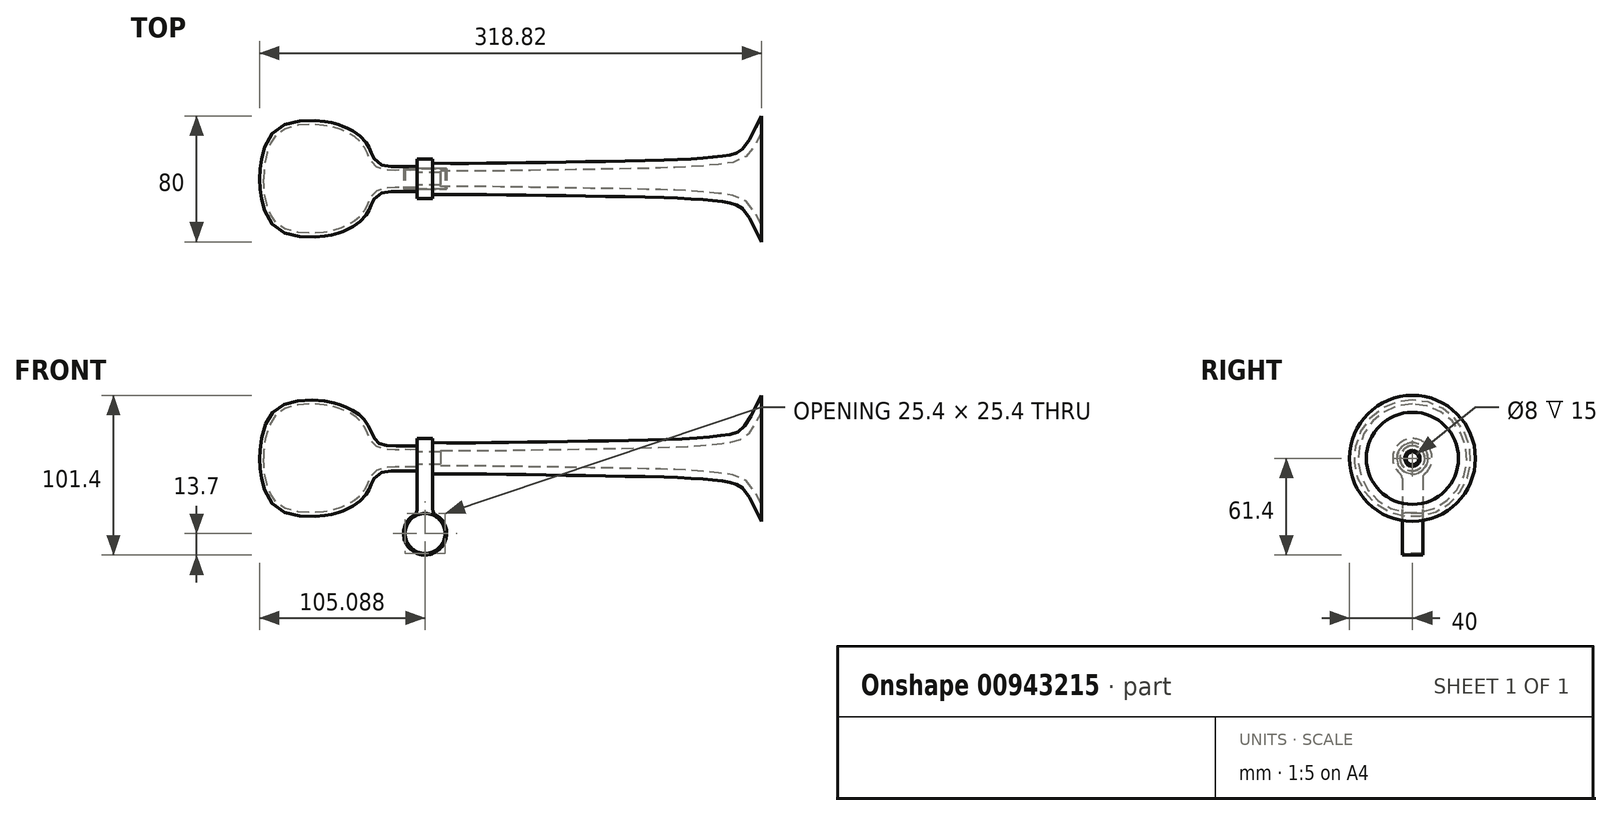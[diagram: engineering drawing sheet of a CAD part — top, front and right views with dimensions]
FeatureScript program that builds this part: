
annotation { "Feature Type Name" : "Feature", "Feature Type Description" : "" }
export const myFeature = defineFeature(function(context is Context, id is Id, definition is map)
    precondition{}
    {
        {
            var Q0;
            Q0=qCreatedBy(makeId("Front.planeOp"),FACE);
            var sketch = newSketch(context, id + "F0", { "sketchPlane" : qUnion([Q0])});
            skLineSegment(sketch, "E0", {"start": v(0, 0) * mm, "end": v(211.18, 0) * mm, "construction": true});
            skLineSegment(sketch, "E1", {"start": v(0, 0) * mm, "end": v(0, 10) * mm});
            skFitSpline(sketch, "E2", {"points": [v(0, 10) * mm, v(36.9, 10) * mm, v(101.92, 11) * mm, v(161.13, 12.56) * mm, v(186.25, 14.85) * mm, v(197.59, 19.9) * mm, v(208.82, 40) * mm, v(215.57, 39.65) * mm], "startDerivative": vector(222.11, -4.41) * mm, "endDerivative": vector(139.53, -179.69) * mm});
            skLineSegment(sketch, "E3", {"start": v(208.82, 40) * mm, "end": v(208.82, 0) * mm});
            skLineSegment(sketch, "E4", {"start": v(0, 0) * mm, "end": v(208.82, 0) * mm});
            skSolve(sketch);
        }
        {
            var Q0;
            Q0=qSketchRegion(id+"F0",true);
            var Q1;
            Q1=sQuery(id+"F0.wireOp",EDGE,"E0");
            revolve(context, id + "F1", {"surfaceOperationType" : NewSurfaceOperationType.NEW, "entities" : qUnion([Q0]), "axis" : qUnion([Q1]), "revolveType" : RevolveType.FULL});
        }
        {
            var Q0;
            Q0=makeQuery(id+"F1.opRevolve","SWEPT_FACE",FACE,{"disambiguationData":[OSD([sQuery(id+"F0.wireOp",EDGE,"E3")])]});
            shell(context, id + "F2", {"entities" : qUnion([Q0]), "thickness" : 5 * mm});
        }
        {
            var Q0;
            Q0=makeQuery(id+"F1.opRevolve","SWEPT_FACE",FACE,{"disambiguationData":[OSD([sQuery(id+"F0.wireOp",EDGE,"E1")])]});
            var sketch = newSketch(context, id + "F3", { "sketchPlane" : qUnion([Q0])});
            skPoint(sketch, "E5", {"position": v(0, 0) * mm});
            skSolve(sketch);
        }
        {
            var Q0;
            Q0=sQuery(id+"F3.wireOp",VERTEX,"E5");
            var Q1;
            Q1=makeQuery(id+"F1.opRevolve","SWEPT_BODY",BODY,{"disambiguationData":[OSD([sQuery(id+"F0.wireOp",EDGE,"E1"),sQuery(id+"F0.wireOp",EDGE,"E2"),sQuery(id+"F0.wireOp",EDGE,"E3"),sQuery(id+"F0.wireOp",EDGE,"E4")])]});
            hole(context, id + "F4", {"style" : HoleStyle.SIMPLE, "endStyle" : HoleEndStyle.THROUGH, "holeDiameter" : 8 * mm, "majorDiameter" : 5 * mm, "isTappedThrough" : true, "tappedDepth" : 12 * mm, "tapClearance" : 3, "locations" : qUnion([Q0]), "scope" : qUnion([Q1])});
        }
        {
            var Q0;
            Q0=makeQuery(id+"F1.opRevolve","SWEPT_FACE",FACE,{"disambiguationData":[OSD([sQuery(id+"F0.wireOp",EDGE,"E1")])]});
            var sketch = newSketch(context, id + "F5", { "sketchPlane" : qUnion([Q0])});
            skCircle(sketch, "E6", {"center": v(0, 0) * mm, "radius": 4 * mm});
            skCircle(sketch, "E7", {"center": v(0, 0) * mm, "radius": 12.5 * mm});
            skSolve(sketch);
        }
        {
            var Q0;
            Q0=qSketchRegion(id+"F5",true);
            extrude(context, id + "F6", {"entities" : qUnion([Q0]), "operationType" : NewBodyOperationType.ADD, "depth" : 10 * mm, "offsetDistance" : 25 * mm});
        }
        {
            var Q0;
            Q0=qCreatedBy(makeId("Front.planeOp"),FACE);
            var sketch = newSketch(context, id + "F7", { "sketchPlane" : qUnion([Q0])});
            skLineSegment(sketch, "E8", {"start": v(0, 0) * mm, "end": v(-66.35, 0) * mm, "construction": true});
            skLineSegment(sketch, "E9", {"start": v(-10, 0) * mm, "end": v(-10, 8) * mm});
            skFitSpline(sketch, "E10", {"points": [v(-10, 8) * mm, v(-18.52, 8) * mm, v(-34.07, 9.5) * mm, v(-39.56, 17.9) * mm, v(-46.2, 27.38) * mm, v(-55.42, 32.65) * mm, v(-65.64, 35.95) * mm, v(-101.42, 29.54) * mm, v(-110, 0) * mm], "startDerivative": vector(-77.46, -10.41) * mm, "endDerivative": vector(0.03, -69.16) * mm});
            skLineSegment(sketch, "E11", {"start": v(-110, 0) * mm, "end": v(-10, 0) * mm});
            skSolve(sketch);
        }
        {
            var Q0;
            Q0=makeQuery(id+"F7.imprint","IMPRINT",FACE,{"disambiguationData":[TD([[makeQuery(id+"F7.imprint","IMPRINT",EDGE,{"derivedFrom":sQuery(id+"F7.wireOp",EDGE,"E9")}),1.0]])]});
            var Q1;
            Q1=sQuery(id+"F7.wireOp",EDGE,"E11");
            revolve(context, id + "F8", {"surfaceOperationType" : NewSurfaceOperationType.NEW, "entities" : qUnion([Q0]), "axis" : qUnion([Q1]), "revolveType" : RevolveType.FULL});
        }
        {
            var Q0;
            Q0=makeQuery(id+"F8.opRevolve","SWEPT_FACE",FACE,{"disambiguationData":[OSD([sQuery(id+"F7.wireOp",EDGE,"E9")])]});
            shell(context, id + "F9", {"entities" : qUnion([Q0]), "thickness" : 2.5 * mm});
        }
        {
            var Q0;
            Q0=qCreatedBy(makeId("Right.planeOp"),FACE);
            var sketch = newSketch(context, id + "F10", { "sketchPlane" : qUnion([Q0])});
            skLineSegment(sketch, "E12.bottom", {"start": v(6.5, -5) * mm, "end": v(-6.5, -5) * mm});
            skLineSegment(sketch, "E12.top", {"start": v(6.5, -35) * mm, "end": v(-6.5, -35) * mm});
            skLineSegment(sketch, "E12.left", {"start": v(6.5, -5) * mm, "end": v(6.5, -35) * mm});
            skLineSegment(sketch, "E12.right", {"start": v(-6.5, -5) * mm, "end": v(-6.5, -35) * mm});
            skPoint(sketch, "E12.middle", {"position": v(0, -20) * mm});
            skSolve(sketch);
        }
        {
            var Q0;
            Q0=qSketchRegion(id+"F10",true);
            extrude(context, id + "F11", {"entities" : qUnion([Q0]), "operationType" : NewBodyOperationType.ADD, "oppositeDirection" : true, "depth" : 10 * mm, "offsetDistance" : 25 * mm});
        }
        {
            var Q0;
            Q0=makeQuery(id+"F11.opExtrude","SWEPT_FACE",FACE,{"disambiguationData":[OSD([sQuery(id+"F10.wireOp",EDGE,"E12.right")])]});
            var sketch = newSketch(context, id + "F12", { "sketchPlane" : qUnion([Q0])});
            skCircle(sketch, "E13", {"center": v(-4.91, -47.7) * mm, "radius": 12.7 * mm});
            skCircle(sketch, "E14", {"center": v(-4.91, -47.7) * mm, "radius": 13.7 * mm});
            skSolve(sketch);
        }
        {
            var Q0;
            Q0=qSketchRegion(id+"F12",true);
            extrude(context, id + "F13", {"entities" : qUnion([Q0]), "operationType" : NewBodyOperationType.ADD, "oppositeDirection" : true, "depth" : 13 * mm, "offsetDistance" : 25 * mm});
        }
        {
            var Q0;
            Q0=makeQuery(id+"F11.boolean.opBoolean","INTERSECT",EDGE,{"derivedFrom":[makeQuery(id+"F6.opExtrude","SWEPT_FACE",FACE,{"disambiguationData":[OSD([sQuery(id+"F5.wireOp",EDGE,"E7")])]}),makeQuery(id+"F11.opExtrude","SWEPT_FACE",FACE,{"disambiguationData":[OSD([sQuery(id+"F10.wireOp",EDGE,"E12.right")])]})]});
            var Q1;
            Q1=makeQuery(id+"F13.boolean.opBoolean","INTERSECT",EDGE,{"derivedFrom":[makeQuery(id+"F11.boolean.opBoolean","MERGE",FACE,{"derivedFrom":[makeQuery(id+"F6.opExtrude","CAP_FACE",FACE,{"disambiguationData":[OSD([sQuery(id+"F5.wireOp",EDGE,"E6"),sQuery(id+"F5.wireOp",EDGE,"E7")])],"isStart":false}),makeQuery(id+"F11.opExtrude","CAP_FACE",FACE,{"disambiguationData":[OSD([sQuery(id+"F10.wireOp",EDGE,"E12.bottom"),sQuery(id+"F10.wireOp",EDGE,"E12.top"),sQuery(id+"F10.wireOp",EDGE,"E12.left"),sQuery(id+"F10.wireOp",EDGE,"E12.right")])],"isStart":false})]}),makeQuery(id+"F13.opExtrude","SWEPT_FACE",FACE,{"disambiguationData":[OSD([sQuery(id+"F12.wireOp",EDGE,"E14")])]})]});
            var Q2;
            Q2=makeQuery(id+"F11.boolean.opBoolean","INTERSECT",EDGE,{"derivedFrom":[makeQuery(id+"F6.opExtrude","SWEPT_FACE",FACE,{"disambiguationData":[OSD([sQuery(id+"F5.wireOp",EDGE,"E7")])]}),makeQuery(id+"F11.opExtrude","SWEPT_FACE",FACE,{"disambiguationData":[OSD([sQuery(id+"F10.wireOp",EDGE,"E12.left")])]})]});
            var Q3;
            Q3=makeQuery(id+"F13.boolean.opBoolean","INTERSECT",EDGE,{"derivedFrom":[makeQuery(id+"F11.boolean.opBoolean","MERGE",FACE,{"derivedFrom":[makeQuery(id+"F6.opExtrude","CAP_FACE",FACE,{"disambiguationData":[OSD([sQuery(id+"F5.wireOp",EDGE,"E6"),sQuery(id+"F5.wireOp",EDGE,"E7")])],"isStart":true}),makeQuery(id+"F11.opExtrude","CAP_FACE",FACE,{"disambiguationData":[OSD([sQuery(id+"F10.wireOp",EDGE,"E12.bottom"),sQuery(id+"F10.wireOp",EDGE,"E12.top"),sQuery(id+"F10.wireOp",EDGE,"E12.left"),sQuery(id+"F10.wireOp",EDGE,"E12.right")])],"isStart":true})]}),makeQuery(id+"F13.opExtrude","SWEPT_FACE",FACE,{"disambiguationData":[OSD([sQuery(id+"F12.wireOp",EDGE,"E14")])]})]});
            fillet(context, id + "F14", {"entities" : qUnion([Q0, Q1, Q2, Q3]), "radius" : 4 * mm, "tangentPropagation" : true, "allowEdgeOverflow" : false});
        }
    });
